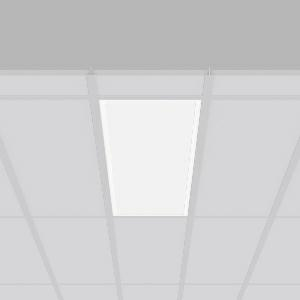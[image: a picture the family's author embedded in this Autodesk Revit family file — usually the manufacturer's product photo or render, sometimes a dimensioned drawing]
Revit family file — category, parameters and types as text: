
# Revit family: sidelite_eco_672370_002_1_89_3848
name_source: partatom
category: Lighting Fixtures
units: mm (PartAtom-declared; Revit-internal decimal feet)

## family parameters
Cut with Voids When Loaded = No
Host = Face
Light Source = No
Part Type = Normal
Room Calculation Point = No
Round Connector Dimension = Use Diameter
Shared = No

## types (1)
- SIDELITE ECO (1 x LED Modul 840, 3550 lm, 4000)
    Apparent Load = 30 VA
    CIE Flux Codes = 46 79 96 100 100
    Color Rendering = 80
    Color Temperature = 4000
    Default Elevation = 1800 mm
    Description = Series: SIDELITE ECO
Highly economical recessed luminaire with progressive LED technology. For escape route illumination. Frame made of aluminium, powder-coated. Diffuser: plastic, opal. Lightguide and diffuser made of non-yellowing plastic (PMMA). Lateral light emission (RZB SIDELITE technology) for homogeneous light distribution. External driver. Second cable inlet for loop through. External driver with simple plug-in locking system. Extended connection cable (1.90 m). With AC Control monitoring module for LUXIFAIR central battery units. Luminaire can be used with accessories (to be ordered separately) for recessed, surface mounting or as pendant luminaire. 
Colour: white
Length: 1195 mm
Width: 295 mm
Cut-out length: 1170 mm
Cut-out width: 270 mm
Recess height: 160 mm
Luminaire: recess height: 40 mm
Weight: 3.94 kg
Operating mode: maintained power mode
Lamp: LED
Socket: without socket
Colour temperature: 4000K
Colour rendering index (CRI): 80
System power: 30 W
Rated luminous flux: 3550 lm
Luminous flux, emergency: 3550 lm
System power, emergency: 30 W
Control gear: Regulated power supply
Protection class: I
Type of protection: IP 20
    Height = 0 mm  [stored 0 ft]
    Lamp = 1 x LED Modul 840
    Lamp Light Flux = 3550 lm
    Lamp count = 1
    Length = 1195 mm
    Lifetime = 50000 h
    Luminous efficacy = 118 lm/W
    Manufacturer = RZB
    ModVariant = No
    Model = 672370.002.1.89
    Mounting Place = Ceiling
    Mounting Type = Recessed
    Number of Poles = 1
    OnlyDefault = Yes
    Power Factor = 1
    Product Name = SIDELITE ECO
    Product group = Recessed modular luminaires
    ProductGroupID = 406
    Protection Class = Protection class I
    Protection Degree = Degree of protection
    RLX_Detail_Level = 1
    RLX_Emergency_Light_Flux = 3550 lm
    RLX_Emergency_Type = 3
    RLX_Emergency_Type_DB = Yes
    RlxData = <blob elided: 31357 chars, md5=5edd6bc1>
    Socket = socket
    Standby Power = 0 W
    System Light Flux = 3550 lm
    System Power = 30 W
    Type Comments = Product without accessories
    Type Image = 312365.002.jpg
    URL = http://relux.com
    VarID = ---
    Voltage = 0 V
    Weight = 0.00 kg
    Width = 295 mm

note: [stored X ft] marks values corroborated as IEEE doubles in the binary element streams (Revit-internal decimal feet)

## geometry (parser evidence)
native form markers: Blend x4, Sweep x10
no freeform markers — native parametric forms only
